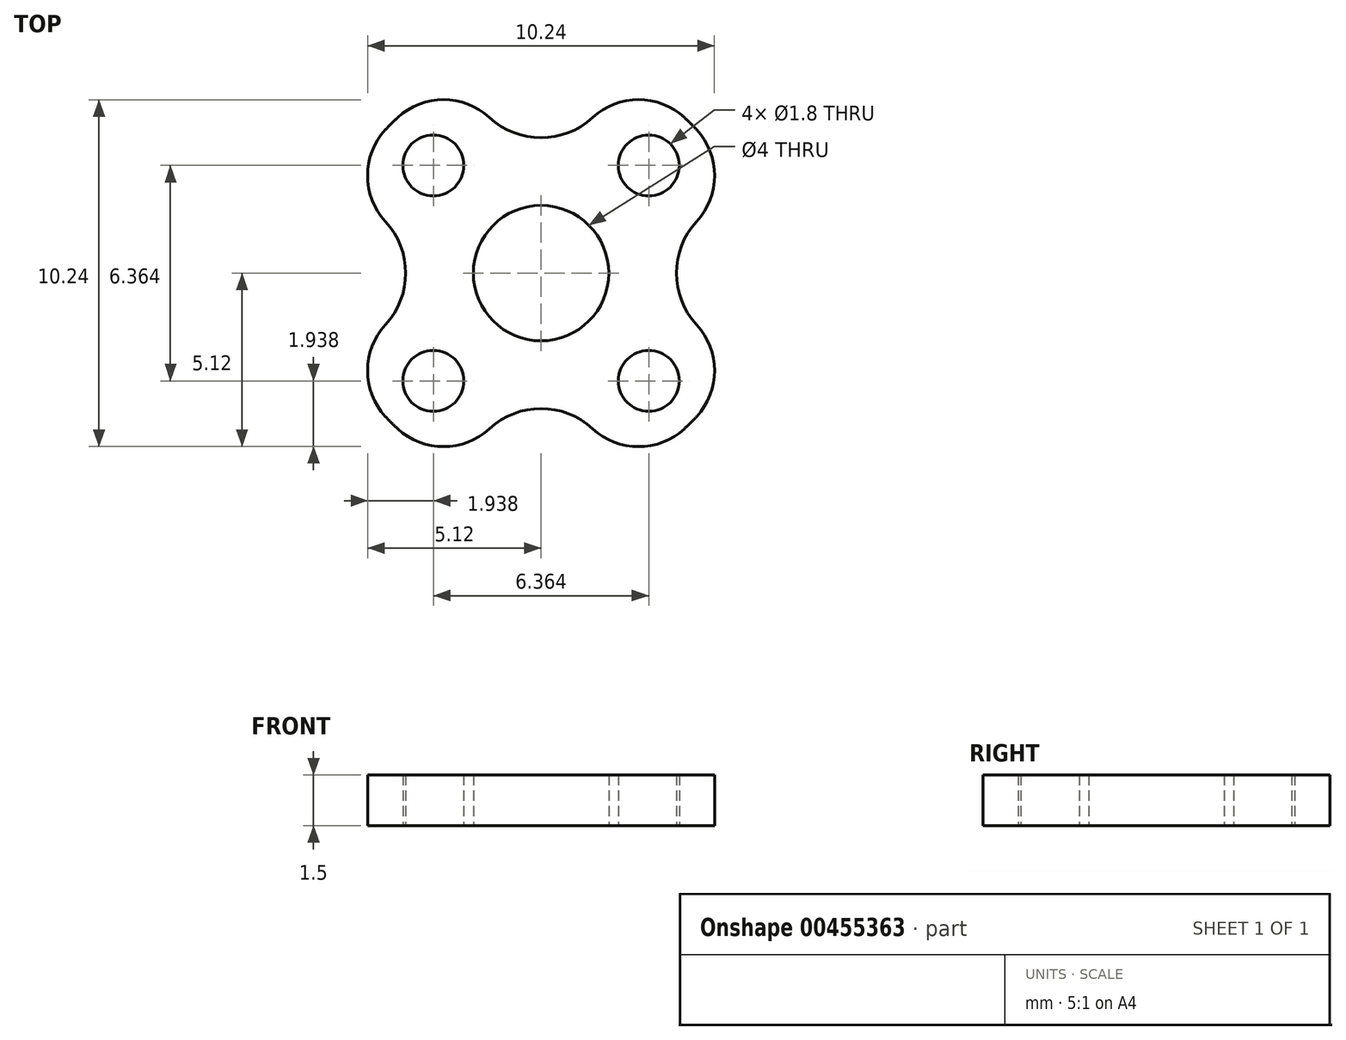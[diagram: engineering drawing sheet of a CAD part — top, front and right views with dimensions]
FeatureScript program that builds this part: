
annotation { "Feature Type Name" : "Feature", "Feature Type Description" : "" }
export const myFeature = defineFeature(function(context is Context, id is Id, definition is map)
    precondition{}
    {
        {
            var Q0;
            Q0=qCreatedBy(makeId("Top.planeOp"),FACE);
            var sketch = newSketch(context, id + "F0", { "sketchPlane" : qUnion([Q0])});
            skCircle(sketch, "E0", {"center": v(0, 0) * mm, "radius": 4.5 * mm, "construction": true});
            skLineSegment(sketch, "E1", {"start": v(0, 0) * mm, "end": v(5.13, 5.13) * mm, "construction": true});
            skCircle(sketch, "E2", {"center": v(3.18, 3.18) * mm, "radius": 0.9 * mm});
            skCircle(sketch, "E3.1.0", {"center": v(-3.18, 3.18) * mm, "radius": 0.9 * mm});
            skCircle(sketch, "E3.2.0", {"center": v(-3.18, -3.18) * mm, "radius": 0.9 * mm});
            skCircle(sketch, "E3.3.0", {"center": v(3.18, -3.18) * mm, "radius": 0.9 * mm});
            skCircle(sketch, "E4", {"center": v(0, 0) * mm, "radius": 2 * mm});
            skArc(sketch, "E5", {"start": v(-2.21, 5.85) * mm, "mid": v(-4.42, 4.42) * mm, "end": v(-5.84, 2.21) * mm});
            skArc(sketch, "E6", {"start": v(-2.21, 5.84) * mm, "mid": v(0, 4) * mm, "end": v(2.21, 5.84) * mm});
            skArc(sketch, "E7.1.0", {"start": v(-5.84, -2.21) * mm, "mid": v(-4, 0) * mm, "end": v(-5.84, 2.21) * mm});
            skArc(sketch, "E7.2.0", {"start": v(2.21, -5.84) * mm, "mid": v(0, -4) * mm, "end": v(-2.21, -5.84) * mm});
            skArc(sketch, "E7.3.0", {"start": v(5.84, 2.21) * mm, "mid": v(4, 0) * mm, "end": v(5.84, -2.21) * mm});
            skArc(sketch, "E8.trimOffspring", {"start": v(5.85, 2.21) * mm, "mid": v(4.42, 4.42) * mm, "end": v(2.21, 5.85) * mm});
            skArc(sketch, "E9.trimOffspring", {"start": v(2.21, -5.85) * mm, "mid": v(4.42, -4.42) * mm, "end": v(5.84, -2.21) * mm});
            skArc(sketch, "E10.trimOffspring", {"start": v(-5.84, -2.21) * mm, "mid": v(-4.42, -4.42) * mm, "end": v(-2.21, -5.84) * mm});
            skSolve(sketch);
        }
        {
            var Q0;
            Q0 = qSketchRegion(id + "F0", true);
            extrude(context, id + "F1", {"entities" : qUnion([Q0]), "depth" : 1.5 * mm});
        }
        {
            var Q0;
            Q0=makeQuery(id+"F1.opExtrude","SWEPT_EDGE",EDGE,{"disambiguationData":[OSD([sQuery(id+"F0.wireOp",EDGE,"E7.2.0"),sQuery(id+"F0.wireOp",EDGE,"E9.trimOffspring")])]});
            var Q1;
            Q1=makeQuery(id+"F1.opExtrude","SWEPT_EDGE",EDGE,{"disambiguationData":[OSD([sQuery(id+"F0.wireOp",EDGE,"E7.2.0"),sQuery(id+"F0.wireOp",EDGE,"E10.trimOffspring")])]});
            var Q2;
            Q2=makeQuery(id+"F1.opExtrude","SWEPT_EDGE",EDGE,{"disambiguationData":[OSD([sQuery(id+"F0.wireOp",EDGE,"E7.3.0"),sQuery(id+"F0.wireOp",EDGE,"E9.trimOffspring")])]});
            var Q3;
            Q3=makeQuery(id+"F1.opExtrude","SWEPT_EDGE",EDGE,{"disambiguationData":[OSD([sQuery(id+"F0.wireOp",EDGE,"E7.3.0"),sQuery(id+"F0.wireOp",EDGE,"E8.trimOffspring")])]});
            var Q4;
            Q4=makeQuery(id+"F1.opExtrude","SWEPT_EDGE",EDGE,{"disambiguationData":[OSD([sQuery(id+"F0.wireOp",EDGE,"E7.1.0"),sQuery(id+"F0.wireOp",EDGE,"E10.trimOffspring")])]});
            var Q5;
            Q5=makeQuery(id+"F1.opExtrude","SWEPT_EDGE",EDGE,{"disambiguationData":[OSD([sQuery(id+"F0.wireOp",EDGE,"E5"),sQuery(id+"F0.wireOp",EDGE,"E6")])]});
            var Q6;
            Q6=makeQuery(id+"F1.opExtrude","SWEPT_EDGE",EDGE,{"disambiguationData":[OSD([sQuery(id+"F0.wireOp",EDGE,"E6"),sQuery(id+"F0.wireOp",EDGE,"E8.trimOffspring")])]});
            var Q7;
            Q7=makeQuery(id+"F1.opExtrude","SWEPT_EDGE",EDGE,{"disambiguationData":[OSD([sQuery(id+"F0.wireOp",EDGE,"E5"),sQuery(id+"F0.wireOp",EDGE,"E7.1.0")])]});
            fillet(context, id + "F2", {"entities" : qUnion([Q0, Q1, Q2, Q3, Q4, Q5, Q6, Q7]), "radius" : 2 * mm, "tangentPropagation" : true, "allowEdgeOverflow" : false});
        }
    });
